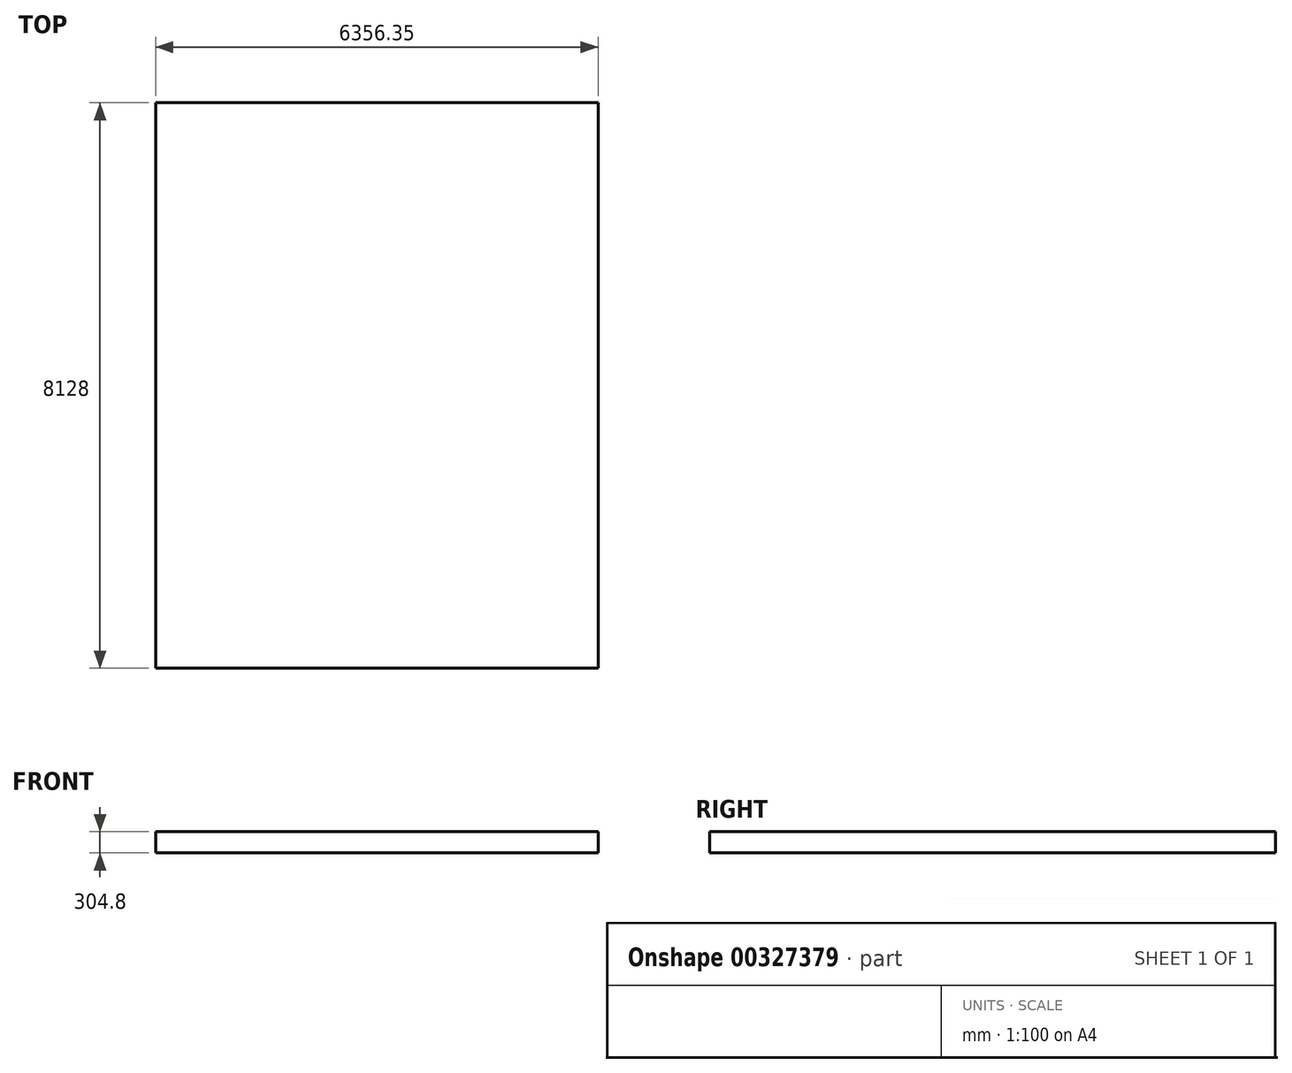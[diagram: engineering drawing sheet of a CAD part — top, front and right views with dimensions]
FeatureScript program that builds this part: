
annotation { "Feature Type Name" : "Feature", "Feature Type Description" : "" }
export const myFeature = defineFeature(function(context is Context, id is Id, definition is map)
    precondition{}
    {
        {
            var Q0;
            Q0=qCreatedBy(makeId("Top.planeOp"),FACE);
            var sketch = newSketch(context, id + "F0", { "sketchPlane" : qUnion([Q0])});
            skLineSegment(sketch, "E0.bottom", {"start": v(0, 0) * mm, "end": v(6356.35, 0) * mm});
            skLineSegment(sketch, "E0.top", {"start": v(0, 8128) * mm, "end": v(6356.35, 8128) * mm});
            skLineSegment(sketch, "E0.left", {"start": v(0, 0) * mm, "end": v(0, 8128) * mm});
            skLineSegment(sketch, "E0.right", {"start": v(6356.35, 0) * mm, "end": v(6356.35, 8128) * mm});
            skSolve(sketch);
        }
        {
            var Q0;
            Q0=makeQuery(id+"F0.imprint","IMPRINT",FACE,{"disambiguationData":[TD([[makeQuery(id+"F0.imprint","IMPRINT",EDGE,{"derivedFrom":sQuery(id+"F0.wireOp",EDGE,"E0.bottom")}),1.0]])]});
            extrude(context, id + "F1", {"entities" : qUnion([Q0]), "oppositeDirection" : true, "depth" : 304.8 * mm});
        }
    });
